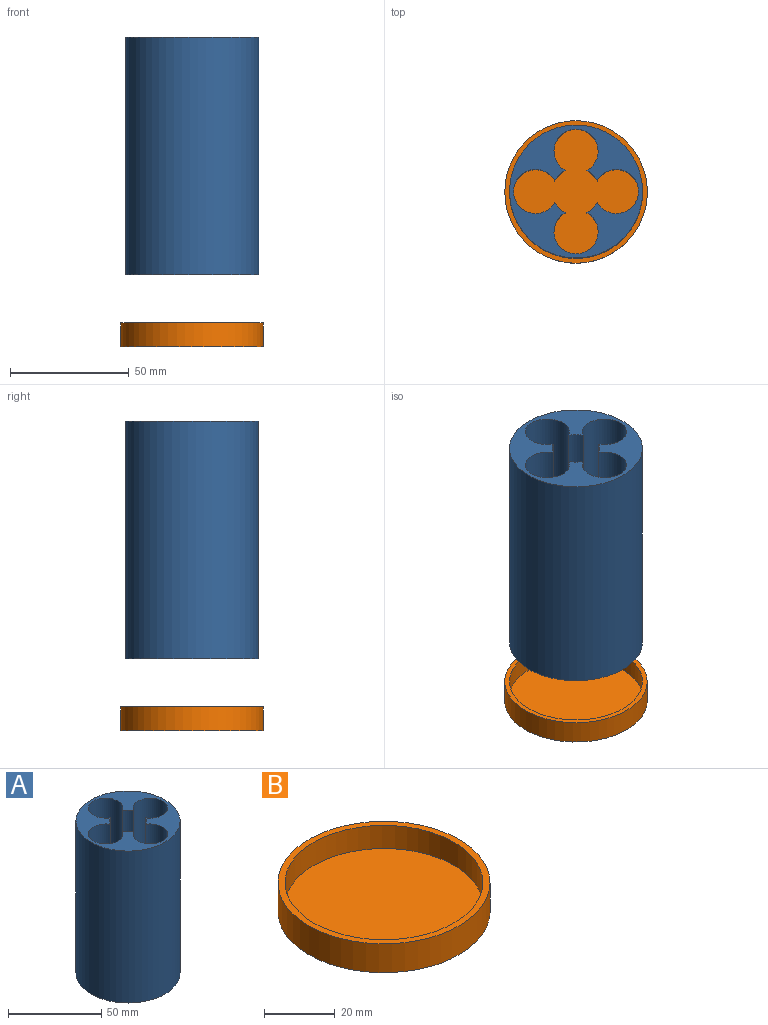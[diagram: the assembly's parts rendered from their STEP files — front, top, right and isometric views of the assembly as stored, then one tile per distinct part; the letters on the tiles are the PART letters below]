
ASSEMBLY  parts=2 mates=1
PART A: 11 faces, bbox 56x56x100 mm
  f0: cylinder r=10mm len=100mm, axis (0,0,-1), area 622.7mm2, adj f5,f6,f9,f10
  f1: cylinder r=10mm len=100mm, axis (0,0,-1), area 622.7mm2, adj f5,f6,f7,f10
  f2: cylinder r=10mm len=100mm, axis (0,0,-1), area 622.7mm2, adj f5,f6,f8,f9
  f3: cylinder r=10mm len=100mm, axis (0,0,-1), area 622.7mm2, adj f5,f6,f7,f8
  f4: cylinder r=28mm len=100mm, axis (0,0,-1), area 17592.9mm2, adj f5,f6
  f5: plane 56x56mm, normal (0,0,1), area 1118.7mm2, adj f0,f1,f2,f3,f4,f7,f8,f9
  f6: plane 56x56mm, normal (0,0,-1), area 1118.7mm2, adj f0,f1,f2,f3,f4,f7,f8,f9
  f7: cylinder r=9.3mm len=100mm, axis (0,0,-1), area 4889.1mm2, adj f1,f3,f5,f6
  f8: cylinder r=9.3mm len=100mm, axis (0,0,-1), area 4889.1mm2, adj f2,f3,f5,f6
  f9: cylinder r=9.3mm len=100mm, axis (0,0,-1), area 4889.1mm2, adj f0,f2,f5,f6
  f10: cylinder r=9.3mm len=100mm, axis (0,0,-1), area 4889.1mm2, adj f0,f1,f5,f6
PART B: 5 faces, bbox 60x60x10 mm
  f0: plane 60x60mm, normal (0,0,-1), area 2827.4mm2, adj f1
  f1: cylinder r=30mm len=60mm, axis (0,0,-1), area 1885mm2, adj f0,f2
  f2: plane 60x60mm, normal (0,0,1), area 364.4mm2, adj f1,f4
  f3: plane 56x56mm, normal (0,0,1), area 2463mm2, adj f4
  f4: cylinder r=28mm len=56mm, axis (0,0,-1), area 1407.4mm2, adj f2,f3
PLACE A t=(-27.32,-21.14,21.62)mm
PLACE B t=(-27.32,-21.14,-8.61)mm
MATE cylindrical B.f1 <-> A.f4  axis (0,0,1) through (-27.32,-21.14,-6.61)mm
